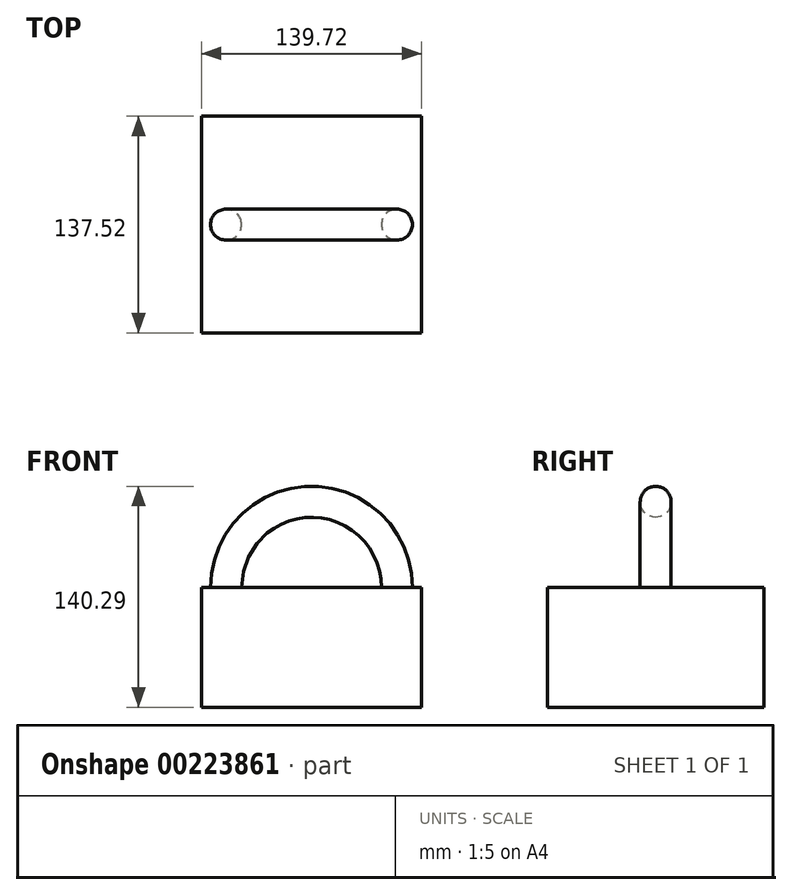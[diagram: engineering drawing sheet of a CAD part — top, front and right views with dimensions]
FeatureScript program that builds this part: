
annotation { "Feature Type Name" : "Feature", "Feature Type Description" : "" }
export const myFeature = defineFeature(function(context is Context, id is Id, definition is map)
    precondition{}
    {
        {
            var Q0;
            Q0=qCreatedBy(makeId("Top.planeOp"),FACE);
            var sketch = newSketch(context, id + "F0", { "sketchPlane" : qUnion([Q0])});
            skLineSegment(sketch, "E0.bottom", {"start": v(69.86, -68.76) * mm, "end": v(-69.86, -68.76) * mm});
            skLineSegment(sketch, "E0.top", {"start": v(69.86, 68.76) * mm, "end": v(-69.86, 68.76) * mm});
            skLineSegment(sketch, "E0.left", {"start": v(69.86, -68.76) * mm, "end": v(69.86, 68.76) * mm});
            skLineSegment(sketch, "E0.right", {"start": v(-69.86, -68.76) * mm, "end": v(-69.86, 68.76) * mm});
            skPoint(sketch, "E0.middle", {"position": v(0, 0) * mm});
            skLineSegment(sketch, "E1", {"start": v(0, 68.76) * mm, "end": v(0, -68.76) * mm});
            skSolve(sketch);
        }
        {
            var Q0;
            Q0=qCreatedBy(makeId("Top.planeOp"),FACE);
            var sketch = newSketch(context, id + "F1", { "sketchPlane" : qUnion([Q0])});
            skCircle(sketch, "E2", {"center": v(54.26, 0) * mm, "radius": 9.82 * mm});
            skSolve(sketch);
        }
        {
            var Q0;
            Q0 = qSketchRegion(id + "F0", true);
            extrude(context, id + "F2", {"entities" : qUnion([Q0]), "oppositeDirection" : true, "depth" : 76.2 * mm});
        }
        {
            var Q0;
            Q0=makeQuery(id+"F1.imprint","IMPRINT",FACE,{"disambiguationData":[TD([[makeQuery(id+"F1.imprint","IMPRINT",EDGE,{"derivedFrom":sQuery(id+"F1.wireOp",EDGE,"E2")}),1.0]])]});
            var Q1;
            Q1=sQuery(id+"F0.wireOp",EDGE,"E1");
            revolve(context, id + "F3", {"operationType" : NewBodyOperationType.ADD, "entities" : qUnion([Q0]), "axis" : qUnion([Q1]), "revolveType" : RevolveType.FULL});
        }
    });
